# Revit family: FXSQ100A
name_source: partatom
category: Mechanical Equipment
revit_build: Autodesk Revit 2017 (Build: 20170816_0615(x64)
units: mm (PartAtom-declared; Revit-internal decimal feet)

## family parameters
Cut with Voids When Loaded = No
Host = Face
OmniClass Number = 23.75.70.17
OmniClass Title = Water Heated and Cooled Terminal Heating and Cooling Units
Part Type = Normal
Room Calculation Point = Yes
Round Connector Dimension = Use Diameter
Shared = No

## types (1)
- FXSQ100A
    Air filter Type = Resin net with mold resistance
    Casing Material = Galvanised steel plate
    Control systems Infrared remote control = BRC4C65
    Control systems Simplified wired remote control for hotel applications = BRC2E52C (heat recovery type) / BRC3E52C (heat pump type)
    Control systems Wired remote control = BRC1E53A / BRC1E53B / BRC1E53C / BRC1D52
    Cooling capacity Nom. kW = 11.2 kW
    Current - 50Hz Maximum fuse amps (MFA) A = 16 A
    Decoration panel Model = -
    Default Elevation = 0 mm  [stored 0 ft]
    Description = Concealed ceiling
    Dimensions Unit Depth mm = 800 mm
    Dimensions Unit Height mm = 245 mm
    Dimensions Unit Width mm = 1,400 mm
    Heating capacity Nom. kW = 12.5 kW
    IfcExportAs = IfcUnitaryEquipmentType
    IfcExportType = AIRCONDITIONINGUNIT
    Installation Manual = http://www.daikineurope.com
    Manufacturer = Daikin Europe N.V.
    Model = VRV
    Piping connections Drain = VP20 (I.D. 20/O.D. 26)
    Piping connections Gas OD mm = 15.9 mm
    Piping connections Liquid OD mm = 9.52 mm
    Power input - 50Hz Cooling Nom. kW = 0.157 kW
    Power input - 50Hz Heating Nom. kW = 0.154 kW
    Power supply Phase/Frequency/Voltage = 1~/50/60/220-240/220 V
    RSen_C_IFC_version = 2x3
    RSen_C_accessory_index = 0
    RSen_C_code_ETIM = Air-conditioning split system – inside unit (evaporator)
    RSen_C_code_ETIM_URL = https://prod.etim-international.com
    RSen_C_code_article = FXSQ100A2VEB
    RSen_C_code_gtin = -
    RSen_C_code_product = FXSQ100A
    RSen_C_code_product_class = FXSQ-A
    RSen_C_content_date_changed = 13/01/2017
    RSen_C_content_date_issue = 13/01/2017
    RSen_C_content_provider = Daikin Europe N.V.
    RSen_C_content_version = v1.0
    RSen_C_description = Concealed ceiling
    RSen_C_diameter_type = OD
    RSen_C_diameter_type_index = 1
    RSen_C_height = 245 mm  [stored 0.803806 ft]
    RSen_C_length = 800 mm  [stored 2.62467 ft]
    RSen_C_license = Creative Commons Attribution NoDerivs (CC-ND)
    RSen_C_license_info = https://tldrlegal.com
    RSen_C_material = RSen_x_rgb 255 255 255 T00 pure white_gen
    RSen_C_model = VRV
    RSen_C_revit_version = 2015
    RSen_C_type = Concealed ceiling unit with medium ESP
    RSen_C_type_comments = Indoor unit
    RSen_C_width = 1400 mm  [stored 4.59318 ft]
    RSen_E_c01_apparent_power = 0 VA
    RSen_E_c01_current = 0 A
    RSen_E_c01_description = c01_el
    RSen_E_c01_division_engine = No
    RSen_E_c01_load_class = Other
    RSen_E_c01_number_of_poles = 1
    RSen_E_c01_power = 0 W
    RSen_E_c01_power_factor = 1
    RSen_E_c01_power_factor_state = Lagging
    RSen_E_c01_system_type = Power - Balanced
    RSen_E_c01_voltage = 230 V
    RSen_E_c01_yes_no = Yes
    RSen_E_c02_description = c02_controls
    RSen_E_c02_yes_no = Yes
    RSen_M_c01_description = c05_return air
    RSen_M_c01_diameter = 0 mm  [stored 0 ft]
    RSen_M_c01_flow_configuration = Preset
    RSen_M_c01_flow_direction = in
    RSen_M_c01_height = 210 mm  [stored 0.688976 ft]
    RSen_M_c01_loss_method = Not Defined
    RSen_M_c01_shape = Rectangular
    RSen_M_c01_system_classification = Return Air
    RSen_M_c01_width = 1354 mm  [stored 4.44226 ft]
    RSen_M_c01_yes_no = Yes
    RSen_M_c02_description = c06_supply air
    RSen_M_c02_diameter = 0 mm  [stored 0 ft]
    RSen_M_c02_flow_configuration = Preset
    RSen_M_c02_flow_direction = Out
    RSen_M_c02_height = 178 mm  [stored 0.58399 ft]
    RSen_M_c02_loss_method = Not Defined
    RSen_M_c02_shape = Rectangular
    RSen_M_c02_system_classification = Supply Air
    RSen_M_c02_width = 1192 mm  [stored 3.91076 ft]
    RSen_M_c02_yes_no = Yes
    RSen_P_c01_description = c02_liquid piping connection
    RSen_P_c01_diameter = 10 mm  [stored 0.0328084 ft]
    RSen_P_c01_diameter_calc = 10 mm  [stored 0.0328084 ft]
    RSen_P_c01_flow_configuration = Preset
    RSen_P_c01_flow_direction = In
    RSen_P_c01_loss_method = Not Defined
    RSen_P_c01_system_classification = Hydronic Supply
    RSen_P_c01_volume_flow = 0.0 L/s
    RSen_P_c01_yes_no = Yes
    RSen_P_c02_description = c03_gas piping connection
    RSen_P_c02_diameter = 16 mm  [stored 0.0524934 ft]
    RSen_P_c02_diameter_calc = 16 mm  [stored 0.0524934 ft]
    RSen_P_c02_flow_configuration = Preset
    RSen_P_c02_flow_direction = Out
    RSen_P_c02_loss_method = Not Defined
    RSen_P_c02_system_classification = Hydronic Return
    RSen_P_c02_volume_flow = 0.0 L/s
    RSen_P_c02_yes_no = Yes
    RSen_P_c03_description = c04_drain piping connection
    RSen_P_c03_diameter = 26 mm
    RSen_P_c03_diameter_calc = 26 mm
    RSen_P_c03_flow_configuration = Fixture Units
    RSen_P_c03_flow_direction = Out
    RSen_P_c03_load_value = 0
    RSen_P_c03_loss_method = Not Defined
    RSen_P_c03_system_classification = Sanitary
    RSen_P_c03_yes_no = Yes
    Refrigerant GWP = 2,087.5
    Refrigerant Type = R-410A
    Sound power level Cooling High/Nom. dBA = -/61 dBA
    Sound pressure level Cooling High/Nom./Low dBA = 36/34/31 dBA
    Sound pressure level Heating High/Nom./Low dBA = 37/34/31 dBA
    Specification Text = https://my.daikin.eu
    TBQ_I Air flow rate_high = 1920.0 m³/h
    TBQ_I Air flow rate_low = 1380.0 m³/h
    TBQ_I Air flow rate_nom = 1620.0 m³/h
    TBQ_I BaseKeynote = 55.10.10.10
    Type Comments = Indoor unit
    URL = www.daikineurope.com
    Weight Unit kg = 46 kg
    ZZZ_Accessory position_X_Length = 0 mm  [stored 0 ft]
    ZZZ_Accessory position_Y_Length = 0 mm  [stored 0 ft]
    ZZZ_Accessory_FamilyType_Mechanical Equipment = GEO_none_daikin : standard
    ZZZ_Accessory_none_FamilyType_Mechanical Equipment = GEO_none_daikin : standard
    ZZZ_Accessory_plane_Integer = 2
    ZZZ_Air flow pattern_FamilyType_Mechanical Equipment = GEO_none_daikin : standard
    ZZZ_Air flow pattern_X coordinate_Length = 0 mm  [stored 0 ft]
    ZZZ_Air flow pattern_Y coordinate_Length = 0 mm  [stored 0 ft]
    ZZZ_Air flow pattern_Z coordinate_Length = 0 mm  [stored 0 ft]
    ZZZ_Air flow pattern_material_Material = RSen_x_rgb 255 128 128 T80 red_gen
    ZZZ_Air flow pattern_plane_Integer = 1
    ZZZ_Air terminal_connector_FamilyType_Air Terminals = AID_none_connector : none_connector
    ZZZ_Angled wall mounted_YesNo = No
    ZZZ_Bounding Box_FamilyType_Mechanical Equipment = GEO_bounding box_daikin : standard
    ZZZ_Ceiling mounted_YesNo = No
    ZZZ_Clearance zone_back_Length = 500 mm  [stored 1.64042 ft]
    ZZZ_Clearance zone_bottom_Length = 45 mm  [stored 0.147638 ft]
    ZZZ_Clearance zone_front_Length = 0 mm  [stored 0 ft]
    ZZZ_Clearance zone_left_Length = 0 mm  [stored 0 ft]
    ZZZ_Clearance zone_material_Material = RSen_x_rgb 255 128 128 T80 red_gen
    ZZZ_Clearance zone_right_Length = 0 mm  [stored 0 ft]
    ZZZ_Clearance zone_top_Length = 10 mm  [stored 0.0328084 ft]
    ZZZ_Component_01_LOD400_FamilyType_Mechanical Equipment = GEO_none_daikin : standard
    ZZZ_Component_01_X_Length = 0 mm  [stored 0 ft]
    ZZZ_Component_01_Y_Length = 0 mm  [stored 0 ft]
    ZZZ_Component_01_Z_Length = 0 mm  [stored 0 ft]
    ZZZ_Component_01_description_Text = -
    ZZZ_Component_01_height_Length = 245 mm  [stored 0.803806 ft]
    ZZZ_Component_01_length_Length = 800 mm  [stored 2.62467 ft]
    ZZZ_Component_01_material_Material = RSen_x_rgb 255 255 255 T00 pure white_gen
    ZZZ_Component_01_plane_Integer = 1
    ZZZ_Component_01_width_Length = 1400 mm  [stored 4.59318 ft]
    ZZZ_Component_02_LOD400_FamilyType_Mechanical Equipment = GEO_none_daikin : standard
    ZZZ_Component_02_X_Length = 0 mm  [stored 0 ft]
    ZZZ_Component_02_Y_Length = 0 mm  [stored 0 ft]
    ZZZ_Component_02_Z_Length = 0 mm  [stored 0 ft]
    ZZZ_Component_02_description_Text = -
    ZZZ_Component_02_height_Length = 0 mm  [stored 0 ft]
    ZZZ_Component_02_length_Length = 0 mm  [stored 0 ft]
    ZZZ_Component_02_material_Material = <By Category>
    ZZZ_Component_02_plane_Integer = 2
    ZZZ_Component_02_width_Length = 0 mm  [stored 0 ft]
    ZZZ_Component_03_X_Length = 0 mm  [stored 0 ft]
    ZZZ_Component_03_Y_Length = 0 mm  [stored 0 ft]
    ZZZ_Component_03_Z_Length = 0 mm  [stored 0 ft]
    ZZZ_Component_03_description_Text = -
    ZZZ_Component_03_height_Length = 0 mm  [stored 0 ft]
    ZZZ_Component_03_length_Length = 0 mm  [stored 0 ft]
    ZZZ_Component_03_material_Material = RSen_x_rgb 255 255 255 T00 pure white_gen
    ZZZ_Component_03_plane_Integer = 0
    ZZZ_Component_03_width_Length = 0 mm  [stored 0 ft]
    ZZZ_Connection zone_back_Length = 0 mm  [stored 0 ft]
    ZZZ_Connection zone_bottom_Length = 0 mm  [stored 0 ft]
    ZZZ_Connection zone_front_Length = 0 mm  [stored 0 ft]
    ZZZ_Connection zone_left_Length = 0 mm  [stored 0 ft]
    ZZZ_Connection zone_material_Material = RSen_x_rgb 255 128 128 T80 red_gen
    ZZZ_Connection zone_right_Length = 0 mm  [stored 0 ft]
    ZZZ_Connection zone_top_Length = 0 mm  [stored 0 ft]
    ZZZ_Cut out_diameter_Length = 0 mm  [stored 0 ft]
    ZZZ_Cut out_height negative_Length = 2 mm  [stored 0.00656168 ft]
    ZZZ_Cut out_height_Length = 0 mm  [stored 0 ft]
    ZZZ_Cut out_length_Length = 0 mm  [stored 0 ft]
    ZZZ_Cut out_length__Length = 1 mm  [stored 0.00328084 ft]
    ZZZ_Cut out_radius_Length = 1 mm  [stored 0.00328084 ft]
    ZZZ_Cut out_width_Length = 0 mm  [stored 0 ft]
    ZZZ_Cut out_width__Length = 1 mm  [stored 0.00328084 ft]
    ZZZ_E_c01_X_Length = 0 mm  [stored 0 ft]
    ZZZ_E_c01_Y_Length = 0 mm  [stored 0 ft]
    ZZZ_E_c01_Z_Length = 0 mm  [stored 0 ft]
    ZZZ_E_c01_plane_Integer = 2
    ZZZ_Flow direction_X_Length = 0 mm  [stored 0 ft]
    ZZZ_Flow direction_Y_Length = 0 mm  [stored 0 ft]
    ZZZ_Flow direction_Z_Length = 0 mm  [stored 0 ft]
    ZZZ_Flow direction_back_YesNo = No
    ZZZ_Flow direction_down_YesNo = No
    ZZZ_Flow direction_front_YesNo = No
    ZZZ_Flow direction_left_YesNo = No
    ZZZ_Flow direction_plane_Integer = 2
    ZZZ_Flow direction_right_YesNo = Yes
    ZZZ_Flow direction_up_YesNo = No
    ZZZ_Grid_height_Length = 600 mm  [stored 1.9685 ft]
    ZZZ_Grid_width_Length = 600 mm  [stored 1.9685 ft]
    ZZZ_Half length negative_Length = -400 mm  [stored -1.31234 ft]
    ZZZ_Half width negative_Length = -700 mm  [stored -2.29659 ft]
    ZZZ_Height negative_Length = -245 mm  [stored -0.803806 ft]
    ZZZ_Height_Length = 245 mm  [stored 0.803806 ft]
    ZZZ_Length_Length = 800 mm  [stored 2.62467 ft]
    ZZZ_Logo_FamilyType_Generic Models = RSen_55_GM_FB_logo - SH_daikin : standard
    ZZZ_Logo_Rotation about axis_Angle = 90.00°
    ZZZ_Logo_X_Length = 0 mm  [stored 0 ft]
    ZZZ_Logo_Y_Length = 0 mm  [stored 0 ft]
    ZZZ_Logo_Z_Length = 0 mm  [stored 0 ft]
    ZZZ_Logo_plane_Integer = 2
    ZZZ_Lookup table name_Text = RSen_55_ME_FB_indoor unit - outdoor unit
    ZZZ_M_c01_X_Length = 0 mm  [stored 0 ft]
    ZZZ_M_c01_Y_Length = 0 mm  [stored 0 ft]
    ZZZ_M_c01_Z_Length = 25 mm  [stored 0.082021 ft]
    ZZZ_M_c01_length_Length = 25 mm  [stored 0.082021 ft]
    ZZZ_M_c01_plane_Integer = 6
    ZZZ_M_c02_X_Length = 50 mm  [stored 0.164042 ft]
    ZZZ_M_c02_Y_Length = -15 mm  [stored -0.0492126 ft]
    ZZZ_M_c02_Z_Length = 25 mm  [stored 0.082021 ft]
    ZZZ_M_c02_length_Length = 25 mm  [stored 0.082021 ft]
    ZZZ_M_c02_plane_Integer = 5
    ZZZ_Maintenance zone_back_Length = 0 mm  [stored 0 ft]
    ZZZ_Maintenance zone_bottom_Length = 0 mm  [stored 0 ft]
    ZZZ_Maintenance zone_front_Length = 0 mm  [stored 0 ft]
    ZZZ_Maintenance zone_left_Length = 0 mm  [stored 0 ft]
    ZZZ_Maintenance zone_material_Material = RSen_x_rgb 255 128 128 T80 red_gen
    ZZZ_Maintenance zone_right_Length = 0 mm  [stored 0 ft]
    ZZZ_Maintenance zone_top_Length = 0 mm  [stored 0 ft]
    ZZZ_Neighbour unit_offset_back_Length = 0 mm  [stored 0 ft]
    ZZZ_Neighbour unit_offset_front_Length = 0 mm  [stored 0 ft]
    ZZZ_Neighbour unit_offset_left_Length = 0 mm  [stored 0 ft]
    ZZZ_Neighbour unit_offset_right_Length = 0 mm  [stored 0 ft]
    ZZZ_P_c01_X_Length = 221 mm  [stored 0.725066 ft]
    ZZZ_P_c01_Y_Length = -14 mm
    ZZZ_P_c01_Z_Length = 69 mm  [stored 0.226378 ft]
    ZZZ_P_c01_length_Length = 70 mm  [stored 0.229659 ft]
    ZZZ_P_c01_plane_Integer = 4
    ZZZ_P_c02_X_Length = 171 mm  [stored 0.561024 ft]
    ZZZ_P_c02_Y_Length = -85 mm
    ZZZ_P_c02_Z_Length = 70 mm  [stored 0.229659 ft]
    ZZZ_P_c02_length_Length = 69 mm  [stored 0.226378 ft]
    ZZZ_P_c02_plane_Integer = 4
    ZZZ_P_c03_X_Length = 99 mm  [stored 0.324803 ft]
    ZZZ_P_c03_Y_Length = -100 mm  [stored -0.328084 ft]
    ZZZ_P_c03_Z_Length = 32 mm  [stored 0.104987 ft]
    ZZZ_P_c03_length_Length = 32 mm  [stored 0.104987 ft]
    ZZZ_P_c03_plane_Integer = 4
    ZZZ_Parallel wall mounted_YesNo = No
    ZZZ_Pendant - horizontal mounted_YesNo = Yes
    ZZZ_Pendant - vertical mounted_YesNo = No
    ZZZ_Placement zone_material_Material = RSen_x_rgb 255 128 128 T80 red_gen
    ZZZ_Recess depth_Length = 0 mm  [stored 0 ft]
    ZZZ_Recess depth_negative_Length = 0 mm  [stored 0 ft]
    ZZZ_Recessed_YesNo = No
    ZZZ_Surface mounted_YesNo = No
    ZZZ_Suspension_YesNo = Yes
    ZZZ_Suspension_length_Length = 630 mm  [stored 2.06693 ft]
    ZZZ_Suspension_offset_Length = 60 mm  [stored 0.19685 ft]
    ZZZ_Suspension_type_FamilyType_Mechanical Equipment = GEO_pendant_gen_witas : Pendant - 2x2 suspension cables_gen
    ZZZ_Suspension_width_Length = 1438 mm  [stored 4.71785 ft]
    ZZZ_Symbol_ceiling_FamilyType_Detail Items = RSen_55_DI_FB_mechanical equipment - none_gen_witas : none_gen
    ZZZ_Symbol_wall_FamilyType_Detail Items = RSen_55_DI_FB_mechanical equipment - none_gen_witas : none_gen
    ZZZ_Total flow rate_HVACAirflow = 0.0 m³/h
    ZZZ_Visualized connectors_FamilyType_Generic Models = RSen_55_GM_FB_none_daikin : standard
    ZZZ_Width_Height_Length = 1400 mm  [stored 4.59318 ft]
    ZZZ_Width_Length = 1400 mm  [stored 4.59318 ft]
    ZZZ_Zones_plane_Integer = 1

note: [stored X ft] marks values corroborated as IEEE doubles in the binary element streams (Revit-internal decimal feet)

## geometry (parser evidence)
native form markers: Sweep x53
no freeform markers — native parametric forms only
